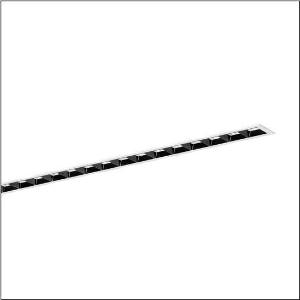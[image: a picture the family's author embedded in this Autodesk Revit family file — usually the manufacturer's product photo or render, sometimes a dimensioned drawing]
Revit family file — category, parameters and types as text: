
# Revit family: silica_r__21_51mx14tbt5w_b174
name_source: partatom
category: Lighting Fixtures
units: mm (PartAtom-declared; Revit-internal decimal feet)

## family parameters
Cut with Voids When Loaded = No
Host = Face
Light Source = No
Part Type = Normal
Room Calculation Point = No
Round Connector Dimension = Use Diameter
Shared = No

## types (1)
- --- (1 x LED, 4100 lm, 40.5 W, 6500K)
    Apparent Load = 41 VA
    CIE Flux Codes = 74 94 99 100 100
    Color Rendering = 80
    Color Temperature = 6500K
    Default Elevation = 1800 mm
    Description = Silica® 21, office luminaire, primary light control with darklight reflector, of PMMA, black, light emission: direct distribution, primary light characteristic: asymmetric, installation type: recessed, LED, rated luminous flux: 4.100lm, luminous efficacy: 96lm/W, light colour: 8tw, colour temperature: 2700..6500K, with terminal, 3+2-pole, max. 2.5mm², mains connection: 220..240V, AC, 50/60Hz, rated input power: 42.6W, luminaire housing, of aluminium, traffic white (RAL 9016), length: 1.528mm, width: 79mm, height: 53mm, protection rating (complete): IP20, insulation class (complete): insulation class I (protective earthing), certification: CE, permissible operating ambient temperature: 0..+35°C, standard: EN 50419, packaging unit: 1 piece
    Height = 0 mm  [stored 0 ft]
    Lamp = 1 x LED
    Lamp Light Flux = 4100 lm
    Lamp Power = 40.5 W
    Lamp count = 1
    Length = 1527 mm
    Luminous efficacy = 101 lm/W
    Manufacturer = Siteco
    ModVariant = No
    Model = 51MX14TBT5W
    Mounting Place = Ceiling
    Mounting Type = Recessed
    Number of Poles = 1
    OnlyDefault = Yes
    Power Factor = 1
    Product Name = Silica® 21
    Product group = office luminaire | ceiling recessed
    ProductGroupID = 401
    Protection Class = Protection class I
    Protection Degree = IP 20
    RLX_Detail_Level = 1
    RLX_Emergency_Light_Flux = 0 lm
    RLX_Emergency_Type = 0
    RLX_Emergency_Type_DB = No
    RlxData = <blob elided: 39417 chars, md5=05455c0a>
    Socket = socket
    Standby Power = 0 W
    System Light Flux = 4100 lm
    System Power = 41 W
    Type Comments = individual setting
    Type Image = l_1297791.jpg
    URL = http://relux.com
    VarID = @adj_071353
    Voltage = 0 V
    Weight = 0.00 kg
    Width = 79 mm

note: [stored X ft] marks values corroborated as IEEE doubles in the binary element streams (Revit-internal decimal feet)

## geometry (parser evidence)
native form markers: Blend x4, Sweep x10
no freeform markers — native parametric forms only
